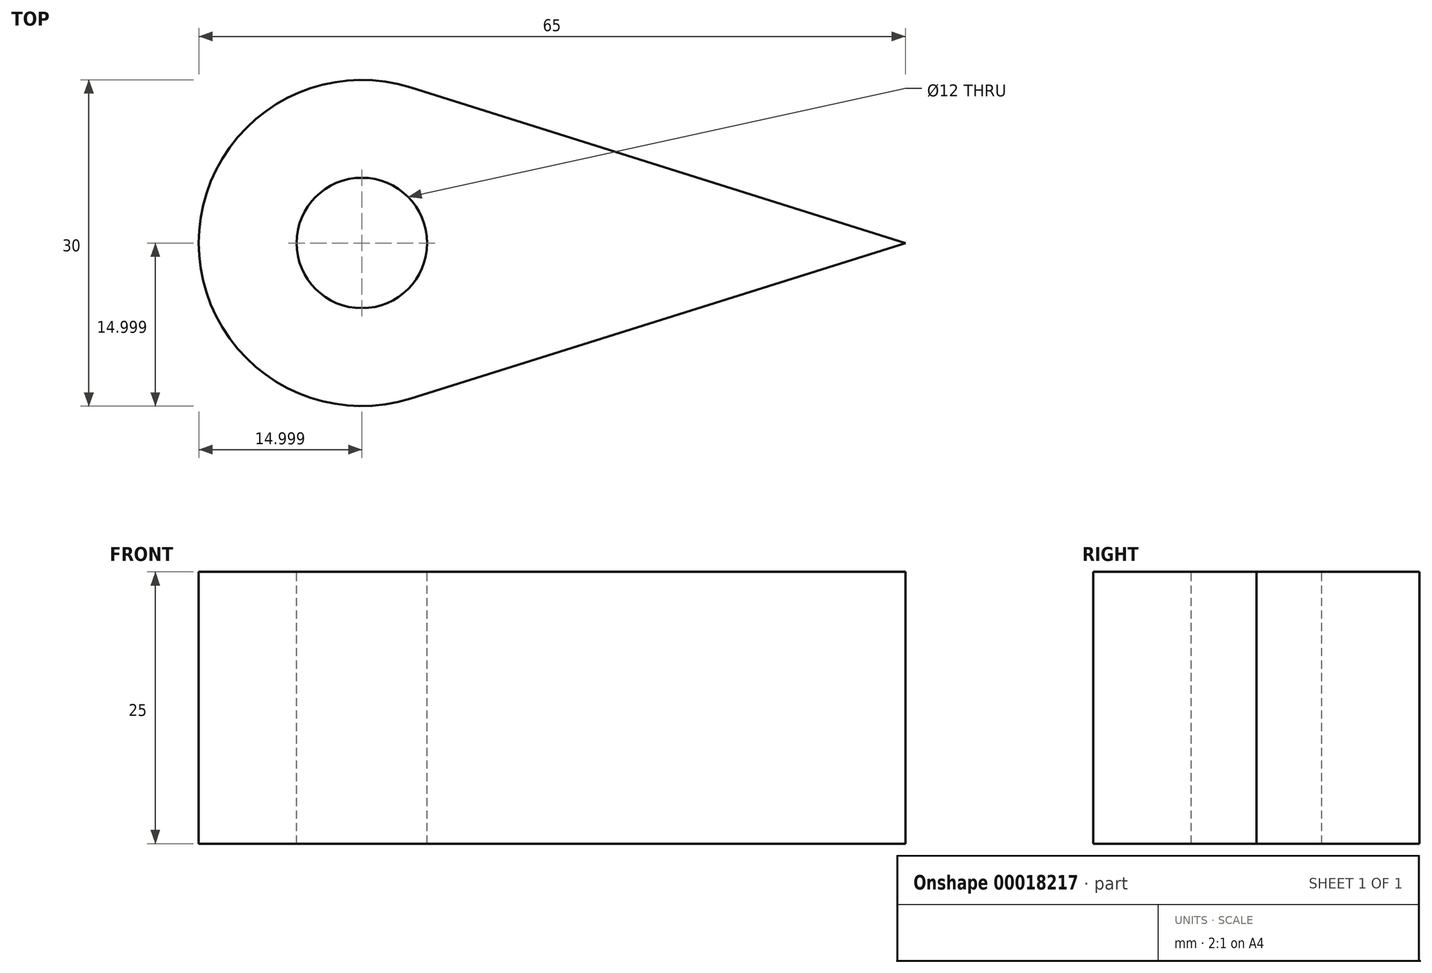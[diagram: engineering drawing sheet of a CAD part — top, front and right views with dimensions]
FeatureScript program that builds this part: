
annotation { "Feature Type Name" : "Feature", "Feature Type Description" : "" }
export const myFeature = defineFeature(function(context is Context, id is Id, definition is map)
    precondition{}
    {
        {
            var Q0;
            Q0=qCreatedBy(makeId("Top.planeOp"),FACE);
            var sketch = newSketch(context, id + "F0", { "sketchPlane" : qUnion([Q0])});
            skArc(sketch, "E0", {"start": v(-29.14, 53.9) * mm, "mid": v(-48.64, 39.59) * mm, "end": v(-29.14, 25.28) * mm});
            skLineSegment(sketch, "E1", {"start": v(-29.14, 25.28) * mm, "end": v(16.36, 39.59) * mm});
            skLineSegment(sketch, "E2", {"start": v(16.36, 39.59) * mm, "end": v(-29.14, 53.9) * mm});
            skSolve(sketch);
        }
        {
            var Q0;
            Q0=makeQuery(id+"F0.imprint","IMPRINT",FACE,{"disambiguationData":[TD([[makeQuery(id+"F0.imprint","IMPRINT",EDGE,{"derivedFrom":sQuery(id+"F0.wireOp",EDGE,"E0")}),1.0]])]});
            extrude(context, id + "F1", {"entities" : qUnion([Q0]), "depth" : 25 * mm});
        }
        {
            var Q0;
            Q0=makeQuery(id+"F1.opExtrude","CAP_FACE",FACE,{"disambiguationData":[OSD([sQuery(id+"F0.wireOp",EDGE,"E0"),sQuery(id+"F0.wireOp",EDGE,"E1"),sQuery(id+"F0.wireOp",EDGE,"E2")])],"isStart":false});
            var sketch = newSketch(context, id + "F2", { "sketchPlane" : qUnion([Q0])});
            skCircle(sketch, "E3", {"center": v(-33.64, 39.59) * mm, "radius": 6 * mm});
            skSolve(sketch);
        }
        {
            var Q0;
            Q0 = qSketchRegion(id + "F2", true);
            extrude(context, id + "F3", {"entities" : qUnion([Q0]), "operationType" : NewBodyOperationType.REMOVE, "endBound" : BoundingType.THROUGH_ALL, "oppositeDirection" : true, "depth" : 25 * mm});
        }
    });
